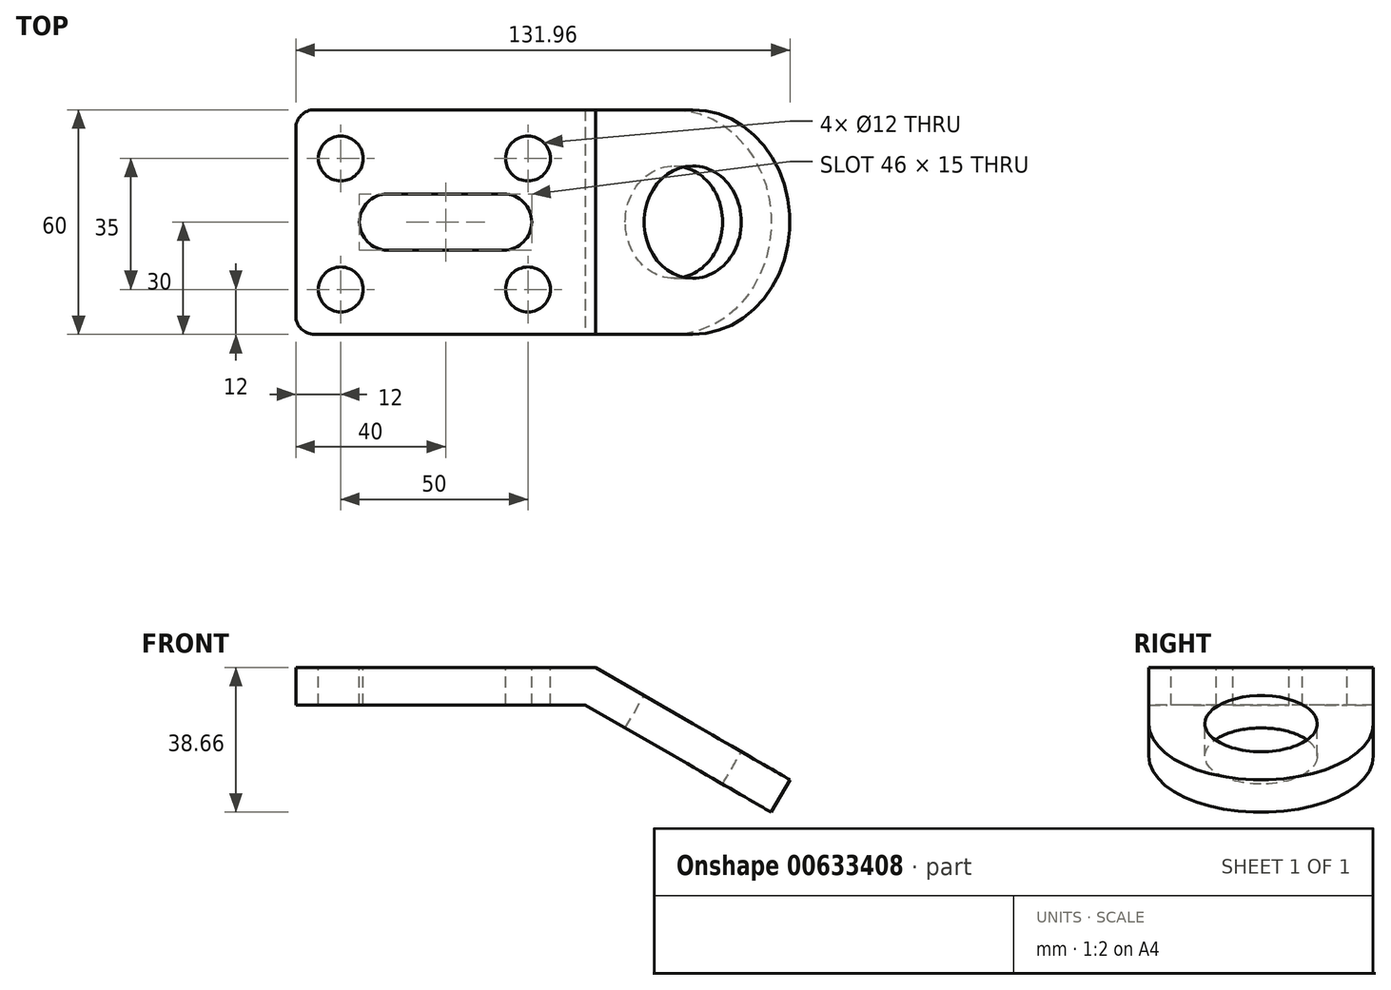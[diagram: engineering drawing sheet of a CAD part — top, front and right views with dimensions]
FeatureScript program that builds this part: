
annotation { "Feature Type Name" : "Feature", "Feature Type Description" : "" }
export const myFeature = defineFeature(function(context is Context, id is Id, definition is map)
    precondition{}
    {
        {
            var Q0;
            Q0=qCreatedBy(makeId("Front.planeOp"),FACE);
            var sketch = newSketch(context, id + "F0", { "sketchPlane" : qUnion([Q0])});
            skLineSegment(sketch, "E0", {"start": v(0, 0) * mm, "end": v(80, 0) * mm});
            skLineSegment(sketch, "E1", {"start": v(80, 0) * mm, "end": v(131.96, -30) * mm});
            skLineSegment(sketch, "E2.0", {"start": v(77.32, -10) * mm, "end": v(126.96, -38.66) * mm});
            skLineSegment(sketch, "E2.1", {"start": v(0, -10) * mm, "end": v(77.32, -10) * mm});
            skLineSegment(sketch, "E3", {"start": v(0, -10) * mm, "end": v(0, 0) * mm});
            skLineSegment(sketch, "E4", {"start": v(126.96, -38.66) * mm, "end": v(131.96, -30) * mm});
            skSolve(sketch);
        }
        {
            var Q0;
            Q0 = qSketchRegion(id + "F0", true);
            extrude(context, id + "F1", {"entities" : qUnion([Q0]), "oppositeDirection" : true, "depth" : 60 * mm, "offsetDistance" : 25 * mm});
        }
        {
            var Q0;
            Q0=makeQuery(id+"F1.opExtrude","CAP_EDGE",EDGE,{"disambiguationData":[OSD([sQuery(id+"F0.wireOp",EDGE,"E4")])],"isStart":true});
            var Q1;
            Q1=makeQuery(id+"F1.opExtrude","CAP_EDGE",EDGE,{"disambiguationData":[OSD([sQuery(id+"F0.wireOp",EDGE,"E4")])],"isStart":false});
            fillet(context, id + "F2", {"entities" : qUnion([Q0, Q1]), "radius" : 30 * mm, "tangentPropagation" : true, "allowEdgeOverflow" : false});
        }
        {
            var Q0;
            Q0=makeQuery(id+"F1.opExtrude","SWEPT_FACE",FACE,{"disambiguationData":[OSD([sQuery(id+"F0.wireOp",EDGE,"E1")])]});
            var sketch = newSketch(context, id + "F3", { "sketchPlane" : qUnion([Q0])});
            skCircle(sketch, "E5", {"center": v(99.28, 30) * mm, "radius": 15 * mm});
            skSolve(sketch);
        }
        {
            var Q0;
            Q0 = qSketchRegion(id + "F3", true);
            extrude(context, id + "F4", {"entities" : qUnion([Q0]), "operationType" : NewBodyOperationType.REMOVE, "endBound" : BoundingType.UP_TO_NEXT, "oppositeDirection" : true, "depth" : 25 * mm, "offsetDistance" : 25 * mm});
        }
        {
            var Q0;
            Q0=makeQuery(id+"F1.opExtrude","SWEPT_FACE",FACE,{"disambiguationData":[OSD([sQuery(id+"F0.wireOp",EDGE,"E0")])]});
            var sketch = newSketch(context, id + "F5", { "sketchPlane" : qUnion([Q0])});
            skCircle(sketch, "E6", {"center": v(12, 12) * mm, "radius": 6 * mm});
            skCircle(sketch, "E7.0.1.0", {"center": v(12, 47) * mm, "radius": 6 * mm});
            skCircle(sketch, "E7.1.0.0", {"center": v(62, 12) * mm, "radius": 6 * mm});
            skCircle(sketch, "E7.1.1.0", {"center": v(62, 47) * mm, "radius": 6 * mm});
            skLineSegment(sketch, "E7.direction1", {"start": v(12, 12) * mm, "end": v(62, 12) * mm, "construction": true});
            skLineSegment(sketch, "E7.direction2", {"start": v(12, 12) * mm, "end": v(12, 47) * mm, "construction": true});
            skSolve(sketch);
        }
        {
            var Q0;
            Q0 = qSketchRegion(id + "F5", true);
            extrude(context, id + "F6", {"entities" : qUnion([Q0]), "operationType" : NewBodyOperationType.REMOVE, "endBound" : BoundingType.UP_TO_NEXT, "oppositeDirection" : true, "depth" : 25 * mm, "offsetDistance" : 25 * mm});
        }
        {
            var Q0;
            Q0=makeQuery(id+"F1.opExtrude","SWEPT_FACE",FACE,{"disambiguationData":[OSD([sQuery(id+"F0.wireOp",EDGE,"E0")])]});
            var sketch = newSketch(context, id + "F7", { "sketchPlane" : qUnion([Q0])});
            skLineSegment(sketch, "E8.bottom", {"start": v(55.5, 22.5) * mm, "end": v(24.5, 22.5) * mm});
            skLineSegment(sketch, "E8.top", {"start": v(55.5, 37.5) * mm, "end": v(24.5, 37.5) * mm});
            skLineSegment(sketch, "E8.left", {"start": v(63, 30) * mm, "end": v(63, 30) * mm});
            skLineSegment(sketch, "E8.right", {"start": v(17, 30) * mm, "end": v(17, 30) * mm});
            skPoint(sketch, "E8.middle", {"position": v(40, 30) * mm});
            skPoint(sketch, "E8.middle.positionSnap0", {"position": v(40, 60) * mm});
            skPoint(sketch, "E8.middle.positionSnap1", {"position": v(0, 30) * mm});
            skPoint(sketch, "E8.centerSnap0", {"position": v(40, 60) * mm});
            skPoint(sketch, "E8.centerSnap1", {"position": v(0, 30) * mm});
            skPoint(sketch, "E9.visualSharp", {"position": v(17, 37.5) * mm});
            skArc(sketch, "E9.filletArc", {"start": v(24.5, 37.5) * mm, "mid": v(19.2, 35.3) * mm, "end": v(17, 30) * mm});
            skPoint(sketch, "E10.visualSharp", {"position": v(17, 22.5) * mm});
            skArc(sketch, "E10.filletArc", {"start": v(17, 30) * mm, "mid": v(19.2, 24.7) * mm, "end": v(24.5, 22.5) * mm});
            skPoint(sketch, "E11.visualSharp", {"position": v(63, 22.5) * mm});
            skArc(sketch, "E11.filletArc", {"start": v(55.5, 22.5) * mm, "mid": v(60.8, 24.7) * mm, "end": v(63, 30) * mm});
            skPoint(sketch, "E12.visualSharp", {"position": v(63, 37.5) * mm});
            skArc(sketch, "E12.filletArc", {"start": v(63, 30) * mm, "mid": v(60.8, 35.3) * mm, "end": v(55.5, 37.5) * mm});
            skSolve(sketch);
        }
        {
            var Q0;
            Q0 = qSketchRegion(id + "F7", true);
            extrude(context, id + "F8", {"entities" : qUnion([Q0]), "operationType" : NewBodyOperationType.REMOVE, "endBound" : BoundingType.UP_TO_NEXT, "oppositeDirection" : true, "depth" : 25 * mm, "offsetDistance" : 25 * mm});
        }
        {
            var Q0;
            Q0=makeQuery(id+"F1.opExtrude","CAP_EDGE",EDGE,{"disambiguationData":[OSD([sQuery(id+"F0.wireOp",EDGE,"E3")])],"isStart":true});
            var Q1;
            Q1=makeQuery(id+"F1.opExtrude","CAP_EDGE",EDGE,{"disambiguationData":[OSD([sQuery(id+"F0.wireOp",EDGE,"E3")])],"isStart":false});
            fillet(context, id + "F9", {"entities" : qUnion([Q0, Q1]), "radius" : 5 * mm, "tangentPropagation" : true, "allowEdgeOverflow" : false});
        }
    });
